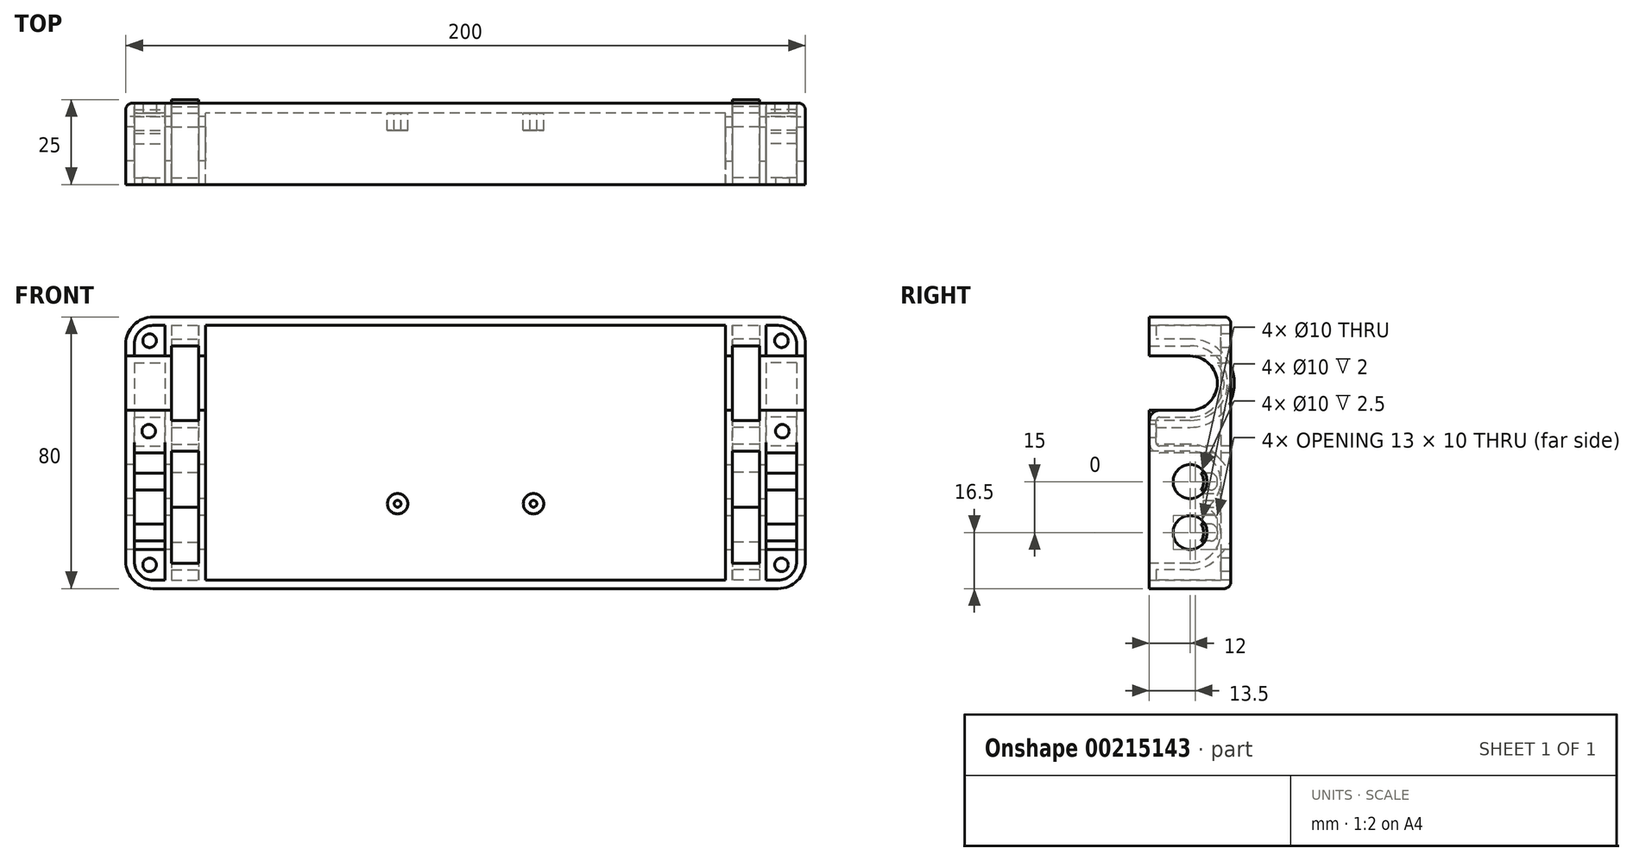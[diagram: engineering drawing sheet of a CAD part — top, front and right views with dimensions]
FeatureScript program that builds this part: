
annotation { "Feature Type Name" : "Feature", "Feature Type Description" : "" }
export const myFeature = defineFeature(function(context is Context, id is Id, definition is map)
    precondition{}
    {
        {
            var Q0;
            Q0=qCreatedBy(makeId("Front.planeOp"),FACE);
            var sketch = newSketch(context, id + "F0", { "sketchPlane" : qUnion([Q0])});
            skLineSegment(sketch, "E0.bottom", {"start": v(92, -40) * mm, "end": v(-92, -40) * mm});
            skLineSegment(sketch, "E0.top", {"start": v(92, 40) * mm, "end": v(-92, 40) * mm});
            skLineSegment(sketch, "E0.left", {"start": v(100, -32) * mm, "end": v(100, 32) * mm});
            skLineSegment(sketch, "E0.right", {"start": v(-100, -32) * mm, "end": v(-100, 32) * mm});
            skPoint(sketch, "E0.middle", {"position": v(0, 0) * mm});
            skPoint(sketch, "E1.visualSharp", {"position": v(-100, 40) * mm});
            skArc(sketch, "E1.filletArc", {"start": v(-92, 40) * mm, "mid": v(-97.66, 37.66) * mm, "end": v(-100, 32) * mm});
            skPoint(sketch, "E2.visualSharp", {"position": v(100, 40) * mm});
            skArc(sketch, "E2.filletArc", {"start": v(100, 32) * mm, "mid": v(97.66, 37.66) * mm, "end": v(92, 40) * mm});
            skPoint(sketch, "E3.visualSharp", {"position": v(100, -40) * mm});
            skArc(sketch, "E3.filletArc", {"start": v(92, -40) * mm, "mid": v(97.66, -37.66) * mm, "end": v(100, -32) * mm});
            skPoint(sketch, "E4.visualSharp", {"position": v(-100, -40) * mm});
            skArc(sketch, "E4.filletArc", {"start": v(-100, -32) * mm, "mid": v(-97.66, -37.66) * mm, "end": v(-92, -40) * mm});
            skSolve(sketch);
        }
        {
            var Q0;
            Q0=makeQuery(id+"F0.imprint","IMPRINT",FACE,{"disambiguationData":[TD([[makeQuery(id+"F0.imprint","IMPRINT",EDGE,{"derivedFrom":sQuery(id+"F0.wireOp",EDGE,"E0.bottom")}),-1.0]])]});
            extrude(context, id + "F1", {"entities" : qUnion([Q0]), "depth" : 24 * mm, "offsetDistance" : 25 * mm});
        }
        {
            var Q0;
            Q0=makeQuery(id+"F1.opExtrude","CAP_FACE",FACE,{"disambiguationData":[OSD([sQuery(id+"F0.wireOp",EDGE,"E0.bottom"),sQuery(id+"F0.wireOp",EDGE,"E0.top"),sQuery(id+"F0.wireOp",EDGE,"E0.left"),sQuery(id+"F0.wireOp",EDGE,"E0.right"),sQuery(id+"F0.wireOp",EDGE,"E1.filletArc"),sQuery(id+"F0.wireOp",EDGE,"E2.filletArc"),sQuery(id+"F0.wireOp",EDGE,"E3.filletArc"),sQuery(id+"F0.wireOp",EDGE,"E4.filletArc")])],"isStart":false});
            var sketch = newSketch(context, id + "F2", { "sketchPlane" : qUnion([Q0])});
            skLineSegment(sketch, "E5.0", {"start": v(97.5, -32) * mm, "end": v(97.5, 32) * mm});
            skArc(sketch, "E5.1", {"start": v(92, -37.5) * mm, "mid": v(95.89, -35.89) * mm, "end": v(97.5, -32) * mm});
            skArc(sketch, "E5.2", {"start": v(97.5, 32) * mm, "mid": v(95.89, 35.89) * mm, "end": v(92, 37.5) * mm});
            skLineSegment(sketch, "E5.3", {"start": v(-92, -37.5) * mm, "end": v(92, -37.5) * mm});
            skLineSegment(sketch, "E5.4", {"start": v(92, 37.5) * mm, "end": v(-92, 37.5) * mm});
            skArc(sketch, "E5.5", {"start": v(-92, 37.5) * mm, "mid": v(-95.89, 35.89) * mm, "end": v(-97.5, 32) * mm});
            skLineSegment(sketch, "E5.6", {"start": v(-97.5, 32) * mm, "end": v(-97.5, -32) * mm});
            skArc(sketch, "E5.7", {"start": v(-97.5, -32) * mm, "mid": v(-95.89, -35.89) * mm, "end": v(-92, -37.5) * mm});
            skSolve(sketch);
        }
        {
            var Q0;
            Q0 = qSketchRegion(id + "F2", true);
            extrude(context, id + "F3", {"entities" : qUnion([Q0]), "operationType" : NewBodyOperationType.REMOVE, "oppositeDirection" : true, "depth" : 21 * mm, "offsetDistance" : 25 * mm});
        }
        {
            var Q0;
            Q0=makeQuery(id+"F1.opExtrude","CAP_EDGE",EDGE,{"disambiguationData":[OSD([sQuery(id+"F0.wireOp",EDGE,"E0.top")])],"isStart":true});
            fillet(context, id + "F4", {"entities" : qUnion([Q0]), "radius" : 2 * mm, "tangentPropagation" : true, "defaultsChanged" : true, "vertexSettings" : [], "allowEdgeOverflow" : false});
        }
        {
            var Q0;
            Q0=makeQuery(id+"F3.boolean.opBoolean","COPY",FACE,{"derivedFrom":makeQuery(id+"F3.opExtrude","CAP_FACE",FACE,{"disambiguationData":[OSD([sQuery(id+"F2.wireOp",EDGE,"E5.0"),sQuery(id+"F2.wireOp",EDGE,"E5.1"),sQuery(id+"F2.wireOp",EDGE,"E5.2"),sQuery(id+"F2.wireOp",EDGE,"E5.3"),sQuery(id+"F2.wireOp",EDGE,"E5.4"),sQuery(id+"F2.wireOp",EDGE,"E5.5"),sQuery(id+"F2.wireOp",EDGE,"E5.6"),sQuery(id+"F2.wireOp",EDGE,"E5.7")])],"isStart":false})});
            var sketch = newSketch(context, id + "F5", { "sketchPlane" : qUnion([Q0])});
            skCircle(sketch, "E6", {"center": v(-93, 33) * mm, "radius": 2 * mm});
            skCircle(sketch, "E7", {"center": v(93, 33) * mm, "radius": 2 * mm});
            skCircle(sketch, "E8", {"center": v(-93, -33) * mm, "radius": 2 * mm});
            skCircle(sketch, "E9", {"center": v(93, -33) * mm, "radius": 2 * mm});
            skLineSegment(sketch, "E10", {"start": v(-97.5, 28.5) * mm, "end": v(-88.5, 28.5) * mm});
            skLineSegment(sketch, "E11", {"start": v(-88.5, 28.5) * mm, "end": v(-88.5, -28.5) * mm});
            skLineSegment(sketch, "E12", {"start": v(-88.5, -28.5) * mm, "end": v(-97.5, -28.5) * mm});
            skLineSegment(sketch, "E13", {"start": v(-97.5, -28.5) * mm, "end": v(-97.5, 28.5) * mm});
            skLineSegment(sketch, "E14", {"start": v(-97.5, 28.5) * mm, "end": v(-97.5, -28.5) * mm});
            skLineSegment(sketch, "E15.MirrorCS", {"start": v(88.5, 28.5) * mm, "end": v(88.5, -28.5) * mm});
            skLineSegment(sketch, "E16.MirrorCS", {"start": v(88.5, -28.5) * mm, "end": v(97.5, -28.5) * mm});
            skLineSegment(sketch, "E17.MirrorCS", {"start": v(97.5, 28.5) * mm, "end": v(97.5, -28.5) * mm});
            skLineSegment(sketch, "E18.MirrorCS", {"start": v(97.5, 28.5) * mm, "end": v(88.5, 28.5) * mm});
            skLineSegment(sketch, "E19", {"start": v(-78.5, -37.5) * mm, "end": v(-78.5, 37.5) * mm});
            skLineSegment(sketch, "E20", {"start": v(-78.5, 37.5) * mm, "end": v(-86.5, 37.5) * mm});
            skLineSegment(sketch, "E21", {"start": v(-86.5, 37.5) * mm, "end": v(-86.5, -37.5) * mm});
            skLineSegment(sketch, "E22", {"start": v(-86.5, -37.5) * mm, "end": v(-78.5, -37.5) * mm});
            skSolve(sketch);
        }
        {
            var Q0;
            Q0 = qSketchRegion(id + "F5", true);
            extrude(context, id + "F6", {"entities" : qUnion([Q0]), "operationType" : NewBodyOperationType.REMOVE, "endBound" : BoundingType.THROUGH_ALL, "oppositeDirection" : true, "depth" : 25 * mm, "offsetDistance" : 25 * mm});
        }
        {
            var Q0;
            Q0=makeQuery(id+"F3.boolean.opBoolean","COPY",FACE,{"derivedFrom":makeQuery(id+"F3.opExtrude","CAP_FACE",FACE,{"disambiguationData":[OSD([sQuery(id+"F2.wireOp",EDGE,"E5.0"),sQuery(id+"F2.wireOp",EDGE,"E5.1"),sQuery(id+"F2.wireOp",EDGE,"E5.2"),sQuery(id+"F2.wireOp",EDGE,"E5.3"),sQuery(id+"F2.wireOp",EDGE,"E5.4"),sQuery(id+"F2.wireOp",EDGE,"E5.5"),sQuery(id+"F2.wireOp",EDGE,"E5.6"),sQuery(id+"F2.wireOp",EDGE,"E5.7")])],"isStart":false})});
            var sketch = newSketch(context, id + "F7", { "sketchPlane" : qUnion([Q0])});
            skLineSegment(sketch, "E23", {"start": v(-88.5, 37.5) * mm, "end": v(-88.5, -37.5) * mm});
            skLineSegment(sketch, "E24", {"start": v(-88.5, 37.5) * mm, "end": v(-86.5, 37.5) * mm});
            skLineSegment(sketch, "E25", {"start": v(-86.5, 37.5) * mm, "end": v(-86.5, -37.5) * mm});
            skLineSegment(sketch, "E26", {"start": v(-86.5, -37.5) * mm, "end": v(-88.5, -37.5) * mm});
            skLineSegment(sketch, "E27.MirrorCS", {"start": v(86.5, 37.5) * mm, "end": v(86.5, -37.5) * mm});
            skLineSegment(sketch, "E28.MirrorCS", {"start": v(88.5, 37.5) * mm, "end": v(88.5, -37.5) * mm});
            skLineSegment(sketch, "E29.MirrorCS", {"start": v(88.5, 37.5) * mm, "end": v(86.5, 37.5) * mm});
            skLineSegment(sketch, "E30.MirrorCS", {"start": v(86.5, -37.5) * mm, "end": v(88.5, -37.5) * mm});
            skLineSegment(sketch, "E31", {"start": v(-78.5, -37.5) * mm, "end": v(-78.5, 37.5) * mm});
            skLineSegment(sketch, "E32", {"start": v(-78.5, 37.5) * mm, "end": v(-76.5, 37.5) * mm});
            skLineSegment(sketch, "E33", {"start": v(-76.5, 37.5) * mm, "end": v(-76.5, -37.5) * mm});
            skLineSegment(sketch, "E34", {"start": v(-76.5, -37.5) * mm, "end": v(-78.5, -37.5) * mm});
            skLineSegment(sketch, "E35.MirrorCS", {"start": v(76.5, 37.5) * mm, "end": v(76.5, -37.5) * mm});
            skLineSegment(sketch, "E36.MirrorCS", {"start": v(78.5, 37.5) * mm, "end": v(76.5, 37.5) * mm});
            skLineSegment(sketch, "E37.MirrorCS", {"start": v(78.5, -37.5) * mm, "end": v(78.5, 37.5) * mm});
            skLineSegment(sketch, "E38.MirrorCS", {"start": v(76.5, -37.5) * mm, "end": v(78.5, -37.5) * mm});
            skSolve(sketch);
        }
        {
            var Q0;
            Q0 = qSketchRegion(id + "F7", true);
            var Q1;
            Q1=makeQuery(id+"F1.opExtrude","CAP_FACE",FACE,{"disambiguationData":[OSD([sQuery(id+"F0.wireOp",EDGE,"E0.bottom"),sQuery(id+"F0.wireOp",EDGE,"E0.top"),sQuery(id+"F0.wireOp",EDGE,"E0.left"),sQuery(id+"F0.wireOp",EDGE,"E0.right"),sQuery(id+"F0.wireOp",EDGE,"E1.filletArc"),sQuery(id+"F0.wireOp",EDGE,"E2.filletArc"),sQuery(id+"F0.wireOp",EDGE,"E3.filletArc"),sQuery(id+"F0.wireOp",EDGE,"E4.filletArc")])],"isStart":false});
            extrude(context, id + "F8", {"entities" : qUnion([Q0]), "operationType" : NewBodyOperationType.ADD, "endBound" : BoundingType.UP_TO_SURFACE, "depth" : 25 * mm, "endBoundEntityFace" : qUnion([Q1]), "offsetDistance" : 25 * mm});
        }
        {
            var Q0;
            Q0=makeQuery(id+"F1.opExtrude","SWEPT_FACE",FACE,{"disambiguationData":[OSD([sQuery(id+"F0.wireOp",EDGE,"E0.right")])]});
            var sketch = newSketch(context, id + "F9", { "sketchPlane" : qUnion([Q0])});
            skArc(sketch, "E39", {"start": v(12, 28.5) * mm, "mid": v(4, 20.5) * mm, "end": v(12, 12.5) * mm});
            skLineSegment(sketch, "E40", {"start": v(12, 28.5) * mm, "end": v(24, 28.5) * mm});
            skLineSegment(sketch, "E41", {"start": v(24, 28.5) * mm, "end": v(24, 12.5) * mm});
            skLineSegment(sketch, "E42", {"start": v(24, 12.5) * mm, "end": v(12, 12.5) * mm});
            skCircle(sketch, "E43", {"center": v(12, -23.5) * mm, "radius": 5 * mm});
            skCircle(sketch, "E44", {"center": v(12, -8.5) * mm, "radius": 5 * mm});
            skSolve(sketch);
        }
        {
            var Q0;
            Q0 = qSketchRegion(id + "F9", true);
            extrude(context, id + "F10", {"entities" : qUnion([Q0]), "operationType" : NewBodyOperationType.REMOVE, "endBound" : BoundingType.THROUGH_ALL, "oppositeDirection" : true, "depth" : 25 * mm, "offsetDistance" : 25 * mm});
        }
        {
            var Q0;
            Q0=makeQuery(id+"F8.boolean.opBoolean","MERGE",FACE,{"derivedFrom":[makeQuery(id+"F6.boolean.opBoolean","COPY",FACE,{"derivedFrom":makeQuery(id+"F6.opExtrude","SWEPT_FACE",FACE,{"disambiguationData":[OSD([sQuery(id+"F5.wireOp",EDGE,"E11")])]})}),makeQuery(id+"F8.opExtrude","SWEPT_FACE",FACE,{"disambiguationData":[OSD([sQuery(id+"F7.wireOp",EDGE,"E23")])]})]});
            var sketch = newSketch(context, id + "F11", { "sketchPlane" : qUnion([Q0])});
            skArc(sketch, "E45", {"start": v(8.88, -21) * mm, "mid": v(8, -23.5) * mm, "end": v(8.88, -26) * mm});
            skLineSegment(sketch, "E46", {"start": v(6, -21) * mm, "end": v(8.88, -21) * mm});
            skPoint(sketch, "E47.start.orphan", {"position": v(8, -23.5) * mm});
            skLineSegment(sketch, "E48", {"start": v(4, -23) * mm, "end": v(4, -24) * mm});
            skLineSegment(sketch, "E49", {"start": v(6, -26) * mm, "end": v(8.88, -26) * mm});
            skPoint(sketch, "E50.visualSharp", {"position": v(4, -21) * mm});
            skArc(sketch, "E50.filletArc", {"start": v(6, -21) * mm, "mid": v(4.59, -21.59) * mm, "end": v(4, -23) * mm});
            skPoint(sketch, "E51.visualSharp", {"position": v(4, -26) * mm});
            skArc(sketch, "E51.filletArc", {"start": v(4, -24) * mm, "mid": v(4.59, -25.41) * mm, "end": v(6, -26) * mm});
            skPoint(sketch, "E52.center.orphan", {"position": v(12, -8.5) * mm});
            skLineSegment(sketch, "E53.MirrorCS", {"start": v(6, -11) * mm, "end": v(8.88, -11) * mm});
            skArc(sketch, "E54.MirrorCS", {"start": v(8.88, -11) * mm, "mid": v(8, -8.5) * mm, "end": v(8.88, -6) * mm});
            skLineSegment(sketch, "E55.MirrorCS", {"start": v(6, -6) * mm, "end": v(8.88, -6) * mm});
            skArc(sketch, "E56.MirrorCS", {"start": v(4, -8) * mm, "mid": v(4.59, -6.59) * mm, "end": v(6, -6) * mm});
            skArc(sketch, "E57.MirrorCS", {"start": v(6, -11) * mm, "mid": v(4.59, -10.41) * mm, "end": v(4, -9) * mm});
            skLineSegment(sketch, "E58.MirrorCS", {"start": v(4, -9) * mm, "end": v(4, -8) * mm});
            skLineSegment(sketch, "E59", {"start": v(0, 0) * mm, "end": v(21, 0) * mm});
            skLineSegment(sketch, "E60", {"start": v(24, 3) * mm, "end": v(24, 9.5) * mm});
            skPoint(sketch, "E61.visualSharp", {"position": v(24, 0) * mm});
            skArc(sketch, "E61.filletArc", {"start": v(21, 0) * mm, "mid": v(23.12, 0.88) * mm, "end": v(24, 3) * mm});
            skPoint(sketch, "E62.visualSharp", {"position": v(24, 12.5) * mm});
            skArc(sketch, "E62.filletArc", {"start": v(24, 9.5) * mm, "mid": v(23.12, 11.62) * mm, "end": v(21, 12.5) * mm});
            skPoint(sketch, "E63.end.orphan", {"position": v(0, 12.5) * mm});
            skLineSegment(sketch, "E64", {"start": v(21, 12.5) * mm, "end": v(12, 12.5) * mm});
            skArc(sketch, "E65.0", {"start": v(12, 28.5) * mm, "mid": v(4, 20.5) * mm, "end": v(12, 12.5) * mm});
            skLineSegment(sketch, "E66", {"start": v(3, 28.5) * mm, "end": v(12, 28.5) * mm});
            skLineSegment(sketch, "E67", {"start": v(3, 28.5) * mm, "end": v(0, 28.5) * mm});
            skLineSegment(sketch, "E68.0", {"start": v(0, 2) * mm, "end": v(21, 2) * mm});
            skArc(sketch, "E68.1", {"start": v(21, 2) * mm, "mid": v(21.7, 2.3) * mm, "end": v(22, 3) * mm});
            skLineSegment(sketch, "E68.2", {"start": v(22, 3) * mm, "end": v(22, 9.5) * mm});
            skArc(sketch, "E68.3", {"start": v(22, 9.5) * mm, "mid": v(21.7, 10.2) * mm, "end": v(21, 10.5) * mm});
            skLineSegment(sketch, "E68.4", {"start": v(3, 26.5) * mm, "end": v(0, 26.5) * mm});
            skLineSegment(sketch, "E68.5", {"start": v(3, 26.5) * mm, "end": v(4, 26.5) * mm});
            skArc(sketch, "E68.6", {"start": v(4, 26.5) * mm, "mid": v(3.06, 16.03) * mm, "end": v(12, 10.5) * mm});
            skLineSegment(sketch, "E68.7", {"start": v(21, 10.5) * mm, "end": v(12, 10.5) * mm});
            skLineSegment(sketch, "E69", {"start": v(0, 0) * mm, "end": v(0, 2) * mm});
            skLineSegment(sketch, "E70", {"start": v(0, 26.5) * mm, "end": v(0, 28.5) * mm});
            skSolve(sketch);
        }
        {
            var Q0;
            Q0 = qSketchRegion(id + "F11", true);
            var Q1;
            Q1=makeQuery(id+"F6.boolean.opBoolean","MERGE",FACE,{"derivedFrom":[makeQuery(id+"F3.boolean.opBoolean","COPY",FACE,{"derivedFrom":makeQuery(id+"F3.opExtrude","SWEPT_FACE",FACE,{"disambiguationData":[OSD([sQuery(id+"F2.wireOp",EDGE,"E5.6")])]})})],"fromTools":[makeQuery(id+"F6.opExtrude","SWEPT_FACE",FACE,{"disambiguationData":[OSD([sQuery(id+"F5.wireOp",EDGE,"E14")])]})]});
            extrude(context, id + "F12", {"entities" : qUnion([Q0]), "operationType" : NewBodyOperationType.ADD, "endBound" : BoundingType.UP_TO_SURFACE, "depth" : 25 * mm, "endBoundEntityFace" : qUnion([Q1]), "offsetDistance" : 25 * mm});
        }
        {
            var Q0;
            Q0=qCreatedBy(makeId("Right.planeOp"),FACE);
            var sketch = newSketch(context, id + "F13", { "sketchPlane" : qUnion([Q0])});
            skLineSegment(sketch, "E71.bottom", {"start": v(-42, 47.28) * mm, "end": v(14.95, 47.28) * mm});
            skLineSegment(sketch, "E71.top", {"start": v(-42, -51.55) * mm, "end": v(14.95, -51.55) * mm});
            skLineSegment(sketch, "E71.left", {"start": v(-42, 47.28) * mm, "end": v(-42, -51.55) * mm});
            skLineSegment(sketch, "E71.right", {"start": v(14.95, 47.28) * mm, "end": v(14.95, -51.55) * mm});
            skSolve(sketch);
        }
        {
            var Q0;
            Q0 = qSketchRegion(id + "F13", true);
            extrude(context, id + "F14", {"entities" : qUnion([Q0]), "operationType" : NewBodyOperationType.REMOVE, "endBound" : BoundingType.THROUGH_ALL, "depth" : 25 * mm, "offsetDistance" : 25 * mm});
        }
        {
            var Q0;
            {var subQ0=sQuery(id+"F0.wireOp",EDGE,"E0.right");var subQ1=sQuery(id+"F9.wireOp",EDGE,"E42");Q0=makeQuery(id+"F10.boolean.opBoolean","COPY",EDGE,{"disambiguationData":[TD([makeQuery(id+"F1.opExtrude","SWEPT_FACE",FACE,{"disambiguationData":[OSD([subQ0])]})])],"derivedFrom":makeQuery(id+"F10.opExtrude","SWEPT_EDGE",EDGE,{"disambiguationData":[OSD([subQ0,sQuery(id+"F9.wireOp",EDGE,"E41"),subQ1])]})});}
            var Q1;
            {var subQ2=sQuery(id+"F0.wireOp",EDGE,"E0.right");var subQ3=sQuery(id+"F9.wireOp",EDGE,"E42");Q1=makeQuery(id+"F10.boolean.opBoolean","COPY",EDGE,{"disambiguationData":[TD([makeQuery(id+"F6.boolean.opBoolean","COPY",FACE,{"derivedFrom":makeQuery(id+"F6.opExtrude","SWEPT_FACE",FACE,{"disambiguationData":[OSD([sQuery(id+"F5.wireOp",EDGE,"E11")])]})})])],"derivedFrom":makeQuery(id+"F10.opExtrude","SWEPT_EDGE",EDGE,{"disambiguationData":[OSD([subQ2,sQuery(id+"F9.wireOp",EDGE,"E41"),subQ3])]})});}
            fillet(context, id + "F15", {"entities" : qUnion([Q0, Q1]), "tangentPropagation" : true, "radius" : 3 * mm, "defaultsChanged" : false, "vertexSettings" : [], "allowEdgeOverflow" : false});
        }
        {
            var Q0;
            {var subQ0=sQuery(id+"F7.wireOp",EDGE,"E25");var subQ1=sQuery(id+"F7.wireOp",EDGE,"E37.MirrorCS");var subQ2=sQuery(id+"F0.wireOp",EDGE,"E4.filletArc");var subQ3=sQuery(id+"F7.wireOp",EDGE,"E33");var subQ4=sQuery(id+"F0.wireOp",EDGE,"E0.bottom");var subQ5=sQuery(id+"F0.wireOp",EDGE,"E0.right");var subQ6=sQuery(id+"F7.wireOp",EDGE,"E31");var subQ7=sQuery(id+"F0.wireOp",EDGE,"E0.left");var subQ8=sQuery(id+"F0.wireOp",EDGE,"E3.filletArc");var subQ9=sQuery(id+"F7.wireOp",EDGE,"E23");var subQ10=sQuery(id+"F7.wireOp",EDGE,"E27.MirrorCS");var subQ11=sQuery(id+"F7.wireOp",EDGE,"E28.MirrorCS");var subQ12=sQuery(id+"F7.wireOp",EDGE,"E35.MirrorCS");var subQ13=makeQuery(id+"F12.boolean.opBoolean","MERGE",FACE,{"derivedFrom":[makeQuery(id+"F10.boolean.opBoolean","SPLIT",FACE,{"disambiguationData":[TD([makeQuery(id+"F1.opExtrude","SWEPT_FACE",FACE,{"disambiguationData":[OSD([subQ4])]})])],"derivedFrom":makeQuery(id+"F8.boolean.opBoolean","MERGE",FACE,{"derivedFrom":[makeQuery(id+"F1.opExtrude","CAP_FACE",FACE,{"disambiguationData":[OSD([subQ4,sQuery(id+"F0.wireOp",EDGE,"E0.top"),subQ7,subQ5,sQuery(id+"F0.wireOp",EDGE,"E1.filletArc"),sQuery(id+"F0.wireOp",EDGE,"E2.filletArc"),subQ8,subQ2])],"isStart":false}),makeQuery(id+"F8.opExtrude","CAP_FACE",FACE,{"disambiguationData":[OSD([subQ9,sQuery(id+"F7.wireOp",EDGE,"E24"),subQ0,sQuery(id+"F7.wireOp",EDGE,"E26")])],"isStart":false}),makeQuery(id+"F8.opExtrude","CAP_FACE",FACE,{"disambiguationData":[OSD([subQ10,subQ11,sQuery(id+"F7.wireOp",EDGE,"E29.MirrorCS"),sQuery(id+"F7.wireOp",EDGE,"E30.MirrorCS")])],"isStart":false}),makeQuery(id+"F8.opExtrude","CAP_FACE",FACE,{"disambiguationData":[OSD([subQ6,sQuery(id+"F7.wireOp",EDGE,"E32"),subQ3,sQuery(id+"F7.wireOp",EDGE,"E34")])],"isStart":false}),makeQuery(id+"F8.opExtrude","CAP_FACE",FACE,{"disambiguationData":[OSD([subQ12,sQuery(id+"F7.wireOp",EDGE,"E36.MirrorCS"),subQ1,sQuery(id+"F7.wireOp",EDGE,"E38.MirrorCS")])],"isStart":false})]})}),makeQuery(id+"F12.opExtrude","SWEPT_FACE",FACE,{"disambiguationData":[OSD([sQuery(id+"F11.wireOp",EDGE,"E60")])]})]});Q0=makeQuery(id+"F22.boolean.opBoolean","MERGE",FACE,{"derivedFrom":[subQ13,makeQuery(id+"F22.opPattern","COPY",FACE,{"derivedFrom":subQ13,"instanceName":"1"})]});}
            var sketch = newSketch(context, id + "F16", { "sketchPlane" : qUnion([Q0])});
            skCircle(sketch, "E72", {"center": v(-93.25, 6.37) * mm, "radius": 2 * mm});
            skSolve(sketch);
        }
        {
            var Q0;
            Q0 = qSketchRegion(id + "F16", true);
            extrude(context, id + "F17", {"entities" : qUnion([Q0]), "operationType" : NewBodyOperationType.REMOVE, "endBound" : BoundingType.THROUGH_ALL, "oppositeDirection" : true, "depth" : 25 * mm, "offsetDistance" : 25 * mm});
        }
        {
            var Q0;
            {var subQ0=sQuery(id+"F2.wireOp",EDGE,"E5.3");var subQ1=sQuery(id+"F2.wireOp",EDGE,"E5.4");var subQ2=makeQuery(id+"F8.boolean.opBoolean","SPLIT",FACE,{"disambiguationData":[TD([makeQuery(id+"F8.opExtrude","SWEPT_FACE",FACE,{"disambiguationData":[OSD([sQuery(id+"F7.wireOp",EDGE,"E33")])]})])],"derivedFrom":makeQuery(id+"F3.boolean.opBoolean","COPY",FACE,{"derivedFrom":makeQuery(id+"F3.opExtrude","CAP_FACE",FACE,{"disambiguationData":[OSD([sQuery(id+"F2.wireOp",EDGE,"E5.0"),sQuery(id+"F2.wireOp",EDGE,"E5.1"),sQuery(id+"F2.wireOp",EDGE,"E5.2"),subQ0,subQ1,sQuery(id+"F2.wireOp",EDGE,"E5.5"),sQuery(id+"F2.wireOp",EDGE,"E5.6"),sQuery(id+"F2.wireOp",EDGE,"E5.7")])],"isStart":false})})});Q0=makeQuery(id+"F22.boolean.opBoolean","MERGE",FACE,{"derivedFrom":[subQ2,makeQuery(id+"F22.opPattern","COPY",FACE,{"derivedFrom":subQ2,"instanceName":"1"})]});}
            var sketch = newSketch(context, id + "F18", { "sketchPlane" : qUnion([Q0])});
            skCircle(sketch, "E73", {"center": v(-20, -15) * mm, "radius": 3 * mm});
            skCircle(sketch, "E74", {"center": v(-20, -15) * mm, "radius": 1 * mm});
            skSolve(sketch);
        }
        {
            var Q0;
            Q0 = qSketchRegion(id + "F18", true);
            extrude(context, id + "F19", {"entities" : qUnion([Q0]), "operationType" : NewBodyOperationType.ADD, "depth" : 5 * mm, "offsetDistance" : 25 * mm});
        }
        {
            var Q0;
            Q0=makeQuery(id+"F8.boolean.opBoolean","MERGE",FACE,{"derivedFrom":[makeQuery(id+"F6.boolean.opBoolean","COPY",FACE,{"derivedFrom":makeQuery(id+"F6.opExtrude","SWEPT_FACE",FACE,{"disambiguationData":[OSD([sQuery(id+"F5.wireOp",EDGE,"E19")])]})}),makeQuery(id+"F8.opExtrude","SWEPT_FACE",FACE,{"disambiguationData":[OSD([sQuery(id+"F7.wireOp",EDGE,"E31")])]})]});
            var sketch = newSketch(context, id + "F20", { "sketchPlane" : qUnion([Q0])});
            skArc(sketch, "E75.0", {"start": v(12, 7.5) * mm, "mid": v(-1, 20.5) * mm, "end": v(12, 33.5) * mm});
            skLineSegment(sketch, "E76", {"start": v(24, 32.5) * mm, "end": v(24, 32.5) * mm});
            skLineSegment(sketch, "E77", {"start": v(12, 9.5) * mm, "end": v(24, 9.5) * mm});
            skLineSegment(sketch, "E78", {"start": v(24, 9.5) * mm, "end": v(24, 7.5) * mm});
            skLineSegment(sketch, "E79", {"start": v(22, 7.5) * mm, "end": v(12, 7.5) * mm});
            skArc(sketch, "E80.0", {"start": v(12, 0.5) * mm, "mid": v(3.38, -5.9) * mm, "end": v(7.03, -16) * mm});
            skArc(sketch, "E81.0", {"start": v(7.03, -16) * mm, "mid": v(3.38, -26.1) * mm, "end": v(12, -32.5) * mm});
            skLineSegment(sketch, "E82", {"start": v(12, -32.5) * mm, "end": v(24, -32.5) * mm});
            skLineSegment(sketch, "E83", {"start": v(12, 0.5) * mm, "end": v(24, 0.5) * mm});
            skLineSegment(sketch, "E84.0", {"start": v(12, 2.5) * mm, "end": v(22, 2.5) * mm});
            skArc(sketch, "E84.1", {"start": v(12, 2.5) * mm, "mid": v(7.33, 1.46) * mm, "end": v(3.55, -1.46) * mm});
            skArc(sketch, "E84.2", {"start": v(3.55, -30.54) * mm, "mid": v(7.33, -33.46) * mm, "end": v(12, -34.5) * mm});
            skLineSegment(sketch, "E84.3", {"start": v(12, -34.5) * mm, "end": v(22, -34.5) * mm});
            skLineSegment(sketch, "E85", {"start": v(3.55, -1.46) * mm, "end": v(0, -5.72) * mm});
            skLineSegment(sketch, "E86", {"start": v(0, -5.72) * mm, "end": v(0, -26.28) * mm});
            skPoint(sketch, "E87.orphan", {"position": v(6.85, 2.5) * mm});
            skLineSegment(sketch, "E88.MirrorCS", {"start": v(3.55, -30.54) * mm, "end": v(0, -26.28) * mm});
            skPoint(sketch, "E89.orphan", {"position": v(0, 0) * mm});
            skLineSegment(sketch, "E90", {"start": v(24, 2.5) * mm, "end": v(24, 0.5) * mm});
            skLineSegment(sketch, "E91", {"start": v(24, -32.5) * mm, "end": v(24, -34.5) * mm});
            skArc(sketch, "E92.0", {"start": v(12, 9.5) * mm, "mid": v(1, 20.5) * mm, "end": v(12, 31.5) * mm});
            skPoint(sketch, "E93.end.orphan", {"position": v(12, 32.5) * mm});
            skLineSegment(sketch, "E94", {"start": v(12, 33.5) * mm, "end": v(22, 33.5) * mm});
            skLineSegment(sketch, "E95", {"start": v(24, 33.5) * mm, "end": v(24, 31.5) * mm});
            skLineSegment(sketch, "E96", {"start": v(24, 31.5) * mm, "end": v(12, 31.5) * mm});
            skLineSegment(sketch, "E97", {"start": v(24, 33.5) * mm, "end": v(24, 37.5) * mm});
            skLineSegment(sketch, "E98", {"start": v(24, 37.5) * mm, "end": v(22, 37.5) * mm});
            skLineSegment(sketch, "E99", {"start": v(22, 37.5) * mm, "end": v(22, 33.5) * mm});
            skLineSegment(sketch, "E100", {"start": v(24, 7.5) * mm, "end": v(24, 2.5) * mm});
            skLineSegment(sketch, "E101", {"start": v(22, 7.5) * mm, "end": v(22, 2.5) * mm});
            skLineSegment(sketch, "E102", {"start": v(24, -34.5) * mm, "end": v(24, -37.5) * mm});
            skLineSegment(sketch, "E103", {"start": v(22, -34.5) * mm, "end": v(22, -37.5) * mm});
            skPoint(sketch, "E104.end.orphan", {"position": v(22.68, -37.5) * mm});
            skLineSegment(sketch, "E105", {"start": v(22, -37.5) * mm, "end": v(24, -37.5) * mm});
            skSolve(sketch);
        }
        {
            var Q0;
            Q0 = qSketchRegion(id + "F20", true);
            var Q1;
            Q1=makeQuery(id+"F8.boolean.opBoolean","MERGE",FACE,{"derivedFrom":[makeQuery(id+"F6.boolean.opBoolean","COPY",FACE,{"derivedFrom":makeQuery(id+"F6.opExtrude","SWEPT_FACE",FACE,{"disambiguationData":[OSD([sQuery(id+"F5.wireOp",EDGE,"E21")])]})}),makeQuery(id+"F8.opExtrude","SWEPT_FACE",FACE,{"disambiguationData":[OSD([sQuery(id+"F7.wireOp",EDGE,"E25")])]})]});
            extrude(context, id + "F21", {"entities" : qUnion([Q0]), "operationType" : NewBodyOperationType.ADD, "endBound" : BoundingType.UP_TO_SURFACE, "depth" : 8 * mm, "endBoundEntityFace" : qUnion([Q1]), "offsetDistance" : 25 * mm});
        }
        {
            var Q0;
            Q0=makeQuery(id+"F1.opExtrude","SWEPT_BODY",BODY,{"disambiguationData":[OSD([sQuery(id+"F0.wireOp",EDGE,"E0.bottom"),sQuery(id+"F0.wireOp",EDGE,"E0.top"),sQuery(id+"F0.wireOp",EDGE,"E0.left"),sQuery(id+"F0.wireOp",EDGE,"E0.right"),sQuery(id+"F0.wireOp",EDGE,"E1.filletArc"),sQuery(id+"F0.wireOp",EDGE,"E2.filletArc"),sQuery(id+"F0.wireOp",EDGE,"E3.filletArc"),sQuery(id+"F0.wireOp",EDGE,"E4.filletArc")])]});
            var Q1;
            Q1=qCreatedBy(makeId("Right.planeOp"),FACE);
            mirror(context, id + "F22", {"operationType" : NewBodyOperationType.ADD, "entities" : qUnion([Q0]), "mirrorPlane" : qUnion([Q1])});
        }
    });
